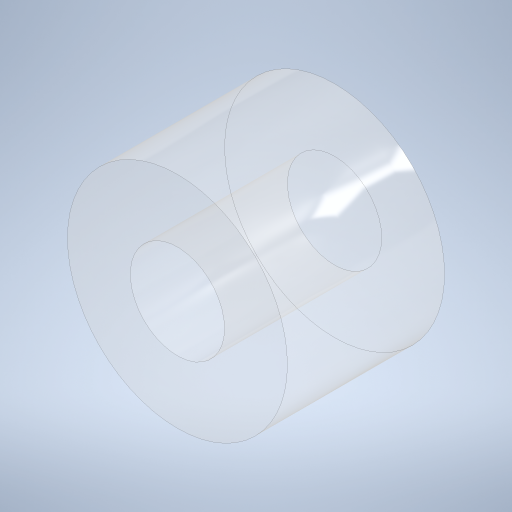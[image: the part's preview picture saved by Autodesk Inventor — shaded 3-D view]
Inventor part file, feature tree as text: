
AUTODESK INVENTOR PART (.ipt)
format: ipt  version: 2023.1 (Build 271208000, 208)  size: 266,240 bytes
history: native  units: mm
features: extrude x1, sketch x1
ambient origin geometry x8: Origin, YZ Plane, XZ Plane, XY Plane, X Axis, Y Axis, Z Axis, Center Point
bodies: Solid1 (feature_tree)
feature tree (2):
  extrude  "Extrusion1"  Depth=5.0mm
  sketch  "Sketch1"  dims[d0=3.0mm d1=7.0mm d2=5.0mm d3=0.0mm]
